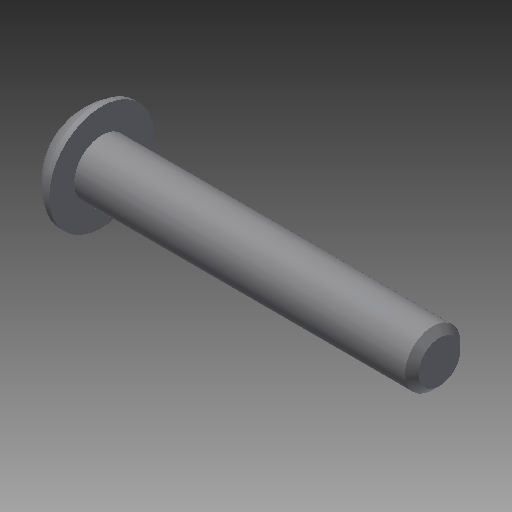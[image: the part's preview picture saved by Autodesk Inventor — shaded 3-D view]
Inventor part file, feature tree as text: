
AUTODESK INVENTOR PART (.ipt)
format: ipt  version: 2017 (Build 210142000, 142)  size: 136,192 bytes
history: native  units: in
note: dims shown in document units (in); Inventor stores cm internally (conversion verified against a paired STEP export)
features: other x2, extrude x1, chamfer x1, imported_body x1, sketch x1
ambient origin geometry x8: Origin, YZ Plane, XZ Plane, XY Plane, X Axis, Y Axis, Z Axis, Center Point
bodies: Body1 (feature_tree)
feature tree (6):
  parser-record x1  (decoder bookkeeping rows leaked as tree rows — omitted from the tree; the rows remain in map.json)
  other  "Bolt"
  extrude  "thread length"  Depth=1.0in TaperAngle=0.0deg
  chamfer  "thread chamfer"  Distance=0.02in Angle=45.0deg
  imported_body  "Base1"
  sketch  "Sketch1"  dims[d0=0.164in d1=1.0in d2=0.0in d3=0.02in d4=0.125in d5=45.0deg d7=0.0in d9=0.0in]
